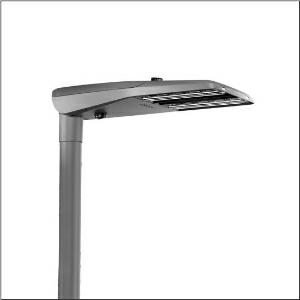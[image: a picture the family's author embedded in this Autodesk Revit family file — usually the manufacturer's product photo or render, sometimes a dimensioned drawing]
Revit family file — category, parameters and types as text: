
# Revit family: streetlight_sl_11_iq_midi___st1_0a_5xc3m51y08le_e71b
name_source: partatom
category: Lighting Fixtures
units: mm (PartAtom-declared; Revit-internal decimal feet)

## family parameters
Cut with Voids When Loaded = No
Host = Face
Light Source = No
Part Type = Normal
Room Calculation Point = No
Round Connector Dimension = Use Diameter
Shared = No

## types (1)
- --- (1 x LED, 8920 lm, 59.4 W, 3000K)
    Apparent Load = 59 VA
    CIE Flux Codes = 33 66 96 100 100
    Color Rendering = 70
    Color Temperature = 3000K
    Default Elevation = 1800 mm
    Description = Streetlight SL 11 iQ midi, mast luminaire, primary light control with 3 zone facetted reflector, of plastic, silver coated, highly specular, primary optical cover: cover, of PMMA, transparent, light distribution: ST1.0a, light emission: direct distribution, primary light characteristic: asymmetric, installation type: post-top, side-entry, lamps: LED, High Power LED, rated values: 8.920lm | 59,4W | 150,2lm/W (begin service life); end service life: 8.920lm | 61,6W; at 50% lumin. flux: 4.460lm | 28,5W | 156,5lm/W, colour temperature: 3000K, colour rendering: CRI > 70, light colour: 730, light setting 1 begin service life: 100% | 8.920lm | 59,4W | 150,2lm/W | 3.000K, light setting 1 end service life: 61,6W, further light settings possible, control: pre-setting: logarithmic dimming characteristic, Street-Remote, Auto-Match, Temp-Guard, Lumen-Switch, Night-Set, Smart-Wire, Light-Fading, Desk-Remote (wireless, voltage-free reading and setting of iQ features in the workshop via application-optimized NFC function/RFID function), optimised constant luminous flux control (CLO 2.0), with cable H07RN-F 5x 1.5mm², mains connection: 230..240V, AC, 50/60Hz, connection cable pre-assembled, cable length: 8,5m, luminaire housing, of diecast aluminium, powder-coated, Siteco® metallic grey (DB 702S), please order mast flange separately, inclination adjustable without tools: 0°, 5°, 10°, 15° (post-top) | 0°, -5°, -10°, -15° (side-entry), sealing non-destructively replaceable, multi-level sealing system, length: 780mm, width: 376mm, height: 118mm, mast flange for spigot size: 42mm (side-entry): 5XC10008XM4, 60/48mm (side-entry/post-top): 5XC10108XM2, 76/60mm (side-entry/post-top): 5XC10108XM1, equipment: standard, Smart Interface below and above, protection rating (complete): IP66, insulation class (complete): insulation class II (safety insulation), certification: CE, ENEC, ENEC+, VDE, UKCA, impact resistance: IK10, permissible operating ambient temperature for outdoor applications: -25..+50°C, standard-compliant lighting for roads and squares, Environmental Product Declaration (EPD) tested and certified by an independent institute, packaging unit: 1 piece

Light Distribution: ST1.0a
    Height = 118 mm
    Lamp = 1 x LED
    Lamp Light Flux = 8920 lm
    Lamp Power = 59.4 W
    Lamp count = 1
    Length = 780 mm
    Luminous efficacy = 150 lm/W
    Manufacturer = Siteco
    ModVariant = No
    Model = 5XC3M51Y08LE
    Number of Poles = 1
    OnlyDefault = Yes
    Power Factor = 1
    Product Name = Streetlight SL 11 iQ midi | ST1.0a
    Product group = mast luminaire | pylon top
    ProductGroupID = 6100
    Protection Class = Protection class II
    Protection Degree = IP 66
    RLX_Detail_Level = 1
    RLX_Emergency_Light_Flux = 0 lm
    RLX_Emergency_Type = 0
    RLX_Emergency_Type_DB = No
    RlxData = <blob elided: 69317 chars, md5=059edc73>
    Socket = socket
    Standby Power = 0 W
    System Light Flux = 8920 lm
    System Power = 59 W
    Type Comments = factory setting: luminous flux: 100 % | dim-lin: 254 | 521 mA
    Type Image = l_1004429.jpg
    URL = http://relux.com
    VarID = @adj_088452
    Voltage = 0 V
    Weight = 0.00 kg
    Width = 376 mm

## geometry (parser evidence)
native form markers: Blend x4, Sweep x10
no freeform markers — native parametric forms only
